# Revit family: Keilhauer_Pact_Bench_360 Unit_77161
name_source: partatom
category: Furniture
revit_build: Autodesk Revit 2017 (Build: 20160225_1515(x64)
units: mm (PartAtom-declared; Revit-internal decimal feet)

## family parameters
Always vertical = Yes
Cut with Voids When Loaded = No
OmniClass Number = 23.40.70.14.64.11
OmniClass Title = Office Furniture
Room Calculation Point = No
Shared = No
Work Plane-Based = No

## types (3) — shared parameters
Assembly Code = E2020200
Catalog = Pact
Manufacturer = Keilhauer, Corp.
Product Documentation Link = http://www.keilhauer.com
URL = http://www.keilhauer.com

## per-type parameters (varying)
| type | Back. | Description | Divider. | Length | Model | Type |
| Backless | No | Pact bench backless 360 unit | No | 3.52 mm  [stored 0.0115486 ft] | 77160 | 1 |
| Dividers | Yes | Pact bench 360 dividers | Yes | 81.1 mm  [stored 0.266076 ft] | 77361 | 3 |
| Back | Yes | Pact bench back 360 unit | No | 66.43 mm  [stored 0.217946 ft] | 77161 | 2 |

note: [stored X ft] marks values corroborated as IEEE doubles in the binary element streams (Revit-internal decimal feet)

## geometry (parser evidence)
native form markers: Sweep x5
no freeform markers — native parametric forms only
